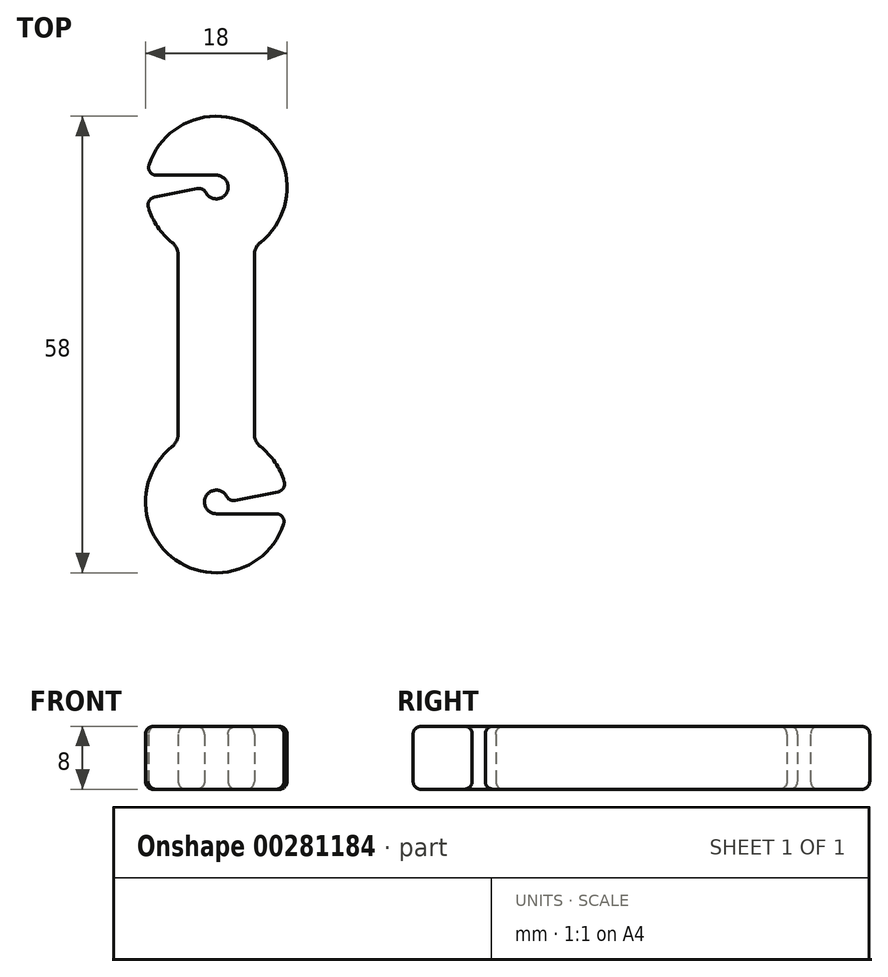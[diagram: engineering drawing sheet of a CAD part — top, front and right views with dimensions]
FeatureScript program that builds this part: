
annotation { "Feature Type Name" : "Feature", "Feature Type Description" : "" }
export const myFeature = defineFeature(function(context is Context, id is Id, definition is map)
    precondition{}
    {
        {
            var Q0;
            Q0=qCreatedBy(makeId("Top.planeOp"),FACE);
            var sketch = newSketch(context, id + "F0", { "sketchPlane" : qUnion([Q0])});
            skArc(sketch, "E0", {"start": v(5.6, 12.95) * mm, "mid": v(5.15, 27.38) * mm, "end": v(-8.55, 22.81) * mm});
            skArc(sketch, "E1.MirrorC", {"start": v(5.6, -12.95) * mm, "mid": v(7.46, -14.96) * mm, "end": v(8.63, -17.44) * mm});
            skLineSegment(sketch, "E2", {"start": v(4.84, 11.38) * mm, "end": v(4.84, -11.38) * mm});
            skLineSegment(sketch, "E3.MirrorCS", {"start": v(-4.84, 11.38) * mm, "end": v(-4.84, -11.38) * mm});
            skArc(sketch, "E4.MirrorC", {"start": v(0, -21.5) * mm, "mid": v(-1.28, -19.22) * mm, "end": v(1.33, -19.3) * mm});
            skArc(sketch, "E5.MirrorC", {"start": v(-1.33, 19.3) * mm, "mid": v(1.28, 19.22) * mm, "end": v(0, 21.5) * mm});
            skLineSegment(sketch, "E6", {"start": v(0, 21.5) * mm, "end": v(-7.6, 21.5) * mm});
            skLineSegment(sketch, "E7", {"start": v(-2.41, 19.81) * mm, "end": v(-7.87, 18.7) * mm});
            skLineSegment(sketch, "E8.MirrorCS", {"start": v(0, -21.5) * mm, "end": v(7.6, -21.5) * mm});
            skLineSegment(sketch, "E9.MirrorCS", {"start": v(2.41, -19.81) * mm, "end": v(7.87, -18.7) * mm});
            skArc(sketch, "E10.trimOffspring", {"start": v(-8.63, 17.44) * mm, "mid": v(-7.46, 14.96) * mm, "end": v(-5.6, 12.95) * mm});
            skArc(sketch, "E11.trimOffspring", {"start": v(8.55, -22.81) * mm, "mid": v(-5.15, -27.38) * mm, "end": v(-5.6, -12.95) * mm});
            skPoint(sketch, "E12.visualSharp", {"position": v(-8.87, 21.5) * mm});
            skArc(sketch, "E12.filletArc", {"start": v(-8.55, 22.81) * mm, "mid": v(-8.4, 21.91) * mm, "end": v(-7.6, 21.5) * mm});
            skPoint(sketch, "E13.visualSharp", {"position": v(8.87, -18.5) * mm});
            skArc(sketch, "E13.filletArc", {"start": v(7.87, -18.7) * mm, "mid": v(8.53, -18.24) * mm, "end": v(8.63, -17.44) * mm});
            skPoint(sketch, "E14.visualSharp", {"position": v(8.87, -21.5) * mm});
            skArc(sketch, "E14.filletArc", {"start": v(8.55, -22.81) * mm, "mid": v(8.4, -21.91) * mm, "end": v(7.6, -21.5) * mm});
            skPoint(sketch, "E15.visualSharp", {"position": v(-8.87, 18.5) * mm});
            skArc(sketch, "E15.filletArc", {"start": v(-7.87, 18.7) * mm, "mid": v(-8.53, 18.24) * mm, "end": v(-8.63, 17.44) * mm});
            skPoint(sketch, "E16.visualSharp", {"position": v(-1.5, 20) * mm});
            skArc(sketch, "E16.filletArc", {"start": v(-1.33, 19.3) * mm, "mid": v(-1.78, 19.74) * mm, "end": v(-2.41, 19.81) * mm});
            skPoint(sketch, "E17.visualSharp", {"position": v(1.5, -20) * mm});
            skArc(sketch, "E17.filletArc", {"start": v(1.33, -19.3) * mm, "mid": v(1.78, -19.74) * mm, "end": v(2.41, -19.81) * mm});
            skPoint(sketch, "E18.visualSharp", {"position": v(-4.84, 12.41) * mm});
            skArc(sketch, "E18.filletArc", {"start": v(-4.84, 11.38) * mm, "mid": v(-5.04, 12.25) * mm, "end": v(-5.6, 12.95) * mm});
            skPoint(sketch, "E19.visualSharp", {"position": v(4.84, 12.41) * mm});
            skArc(sketch, "E19.filletArc", {"start": v(5.6, 12.95) * mm, "mid": v(5.04, 12.25) * mm, "end": v(4.84, 11.38) * mm});
            skPoint(sketch, "E20.visualSharp", {"position": v(-4.84, -12.41) * mm});
            skArc(sketch, "E20.filletArc", {"start": v(-5.6, -12.95) * mm, "mid": v(-5.04, -12.25) * mm, "end": v(-4.84, -11.38) * mm});
            skPoint(sketch, "E21.visualSharp", {"position": v(4.84, -12.41) * mm});
            skArc(sketch, "E21.filletArc", {"start": v(4.84, -11.38) * mm, "mid": v(5.04, -12.25) * mm, "end": v(5.6, -12.95) * mm});
            skSolve(sketch);
        }
        {
            var Q0;
            Q0=makeQuery(id+"F0.imprint","IMPRINT",FACE,{"disambiguationData":[TD([[makeQuery(id+"F0.imprint","IMPRINT",EDGE,{"derivedFrom":sQuery(id+"F0.wireOp",EDGE,"E0")}),1.0]])]});
            extrude(context, id + "F1", {"entities" : qUnion([Q0]), "depth" : 8 * mm});
        }
        {
            var Q0;
            Q0=makeQuery(id+"F1.opExtrude","CAP_FACE",FACE,{"disambiguationData":[OSD([sQuery(id+"F0.wireOp",EDGE,"E0"),sQuery(id+"F0.wireOp",EDGE,"E1.MirrorC"),sQuery(id+"F0.wireOp",EDGE,"E2"),sQuery(id+"F0.wireOp",EDGE,"E3.MirrorCS"),sQuery(id+"F0.wireOp",EDGE,"E4.MirrorC"),sQuery(id+"F0.wireOp",EDGE,"E5.MirrorC"),sQuery(id+"F0.wireOp",EDGE,"E6"),sQuery(id+"F0.wireOp",EDGE,"E7"),sQuery(id+"F0.wireOp",EDGE,"E8.MirrorCS"),sQuery(id+"F0.wireOp",EDGE,"E9.MirrorCS"),sQuery(id+"F0.wireOp",EDGE,"E10.trimOffspring"),sQuery(id+"F0.wireOp",EDGE,"E11.trimOffspring"),sQuery(id+"F0.wireOp",EDGE,"E12.filletArc"),sQuery(id+"F0.wireOp",EDGE,"E13.filletArc"),sQuery(id+"F0.wireOp",EDGE,"E14.filletArc"),sQuery(id+"F0.wireOp",EDGE,"E15.filletArc"),sQuery(id+"F0.wireOp",EDGE,"E16.filletArc"),sQuery(id+"F0.wireOp",EDGE,"E17.filletArc"),sQuery(id+"F0.wireOp",EDGE,"E18.filletArc"),sQuery(id+"F0.wireOp",EDGE,"E19.filletArc"),sQuery(id+"F0.wireOp",EDGE,"E20.filletArc"),sQuery(id+"F0.wireOp",EDGE,"E21.filletArc")])],"isStart":false});
            var Q1;
            Q1=makeQuery(id+"F1.opExtrude","CAP_FACE",FACE,{"disambiguationData":[OSD([sQuery(id+"F0.wireOp",EDGE,"E0"),sQuery(id+"F0.wireOp",EDGE,"E1.MirrorC"),sQuery(id+"F0.wireOp",EDGE,"E2"),sQuery(id+"F0.wireOp",EDGE,"E3.MirrorCS"),sQuery(id+"F0.wireOp",EDGE,"E4.MirrorC"),sQuery(id+"F0.wireOp",EDGE,"E5.MirrorC"),sQuery(id+"F0.wireOp",EDGE,"E6"),sQuery(id+"F0.wireOp",EDGE,"E7"),sQuery(id+"F0.wireOp",EDGE,"E8.MirrorCS"),sQuery(id+"F0.wireOp",EDGE,"E9.MirrorCS"),sQuery(id+"F0.wireOp",EDGE,"E10.trimOffspring"),sQuery(id+"F0.wireOp",EDGE,"E11.trimOffspring"),sQuery(id+"F0.wireOp",EDGE,"E12.filletArc"),sQuery(id+"F0.wireOp",EDGE,"E13.filletArc"),sQuery(id+"F0.wireOp",EDGE,"E14.filletArc"),sQuery(id+"F0.wireOp",EDGE,"E15.filletArc"),sQuery(id+"F0.wireOp",EDGE,"E16.filletArc"),sQuery(id+"F0.wireOp",EDGE,"E17.filletArc"),sQuery(id+"F0.wireOp",EDGE,"E18.filletArc"),sQuery(id+"F0.wireOp",EDGE,"E19.filletArc"),sQuery(id+"F0.wireOp",EDGE,"E20.filletArc"),sQuery(id+"F0.wireOp",EDGE,"E21.filletArc")])],"isStart":true});
            fillet(context, id + "F2", {"entities" : qUnion([Q0, Q1]), "radius" : 1 * mm, "tangentPropagation" : true, "allowEdgeOverflow" : false});
        }
    });
